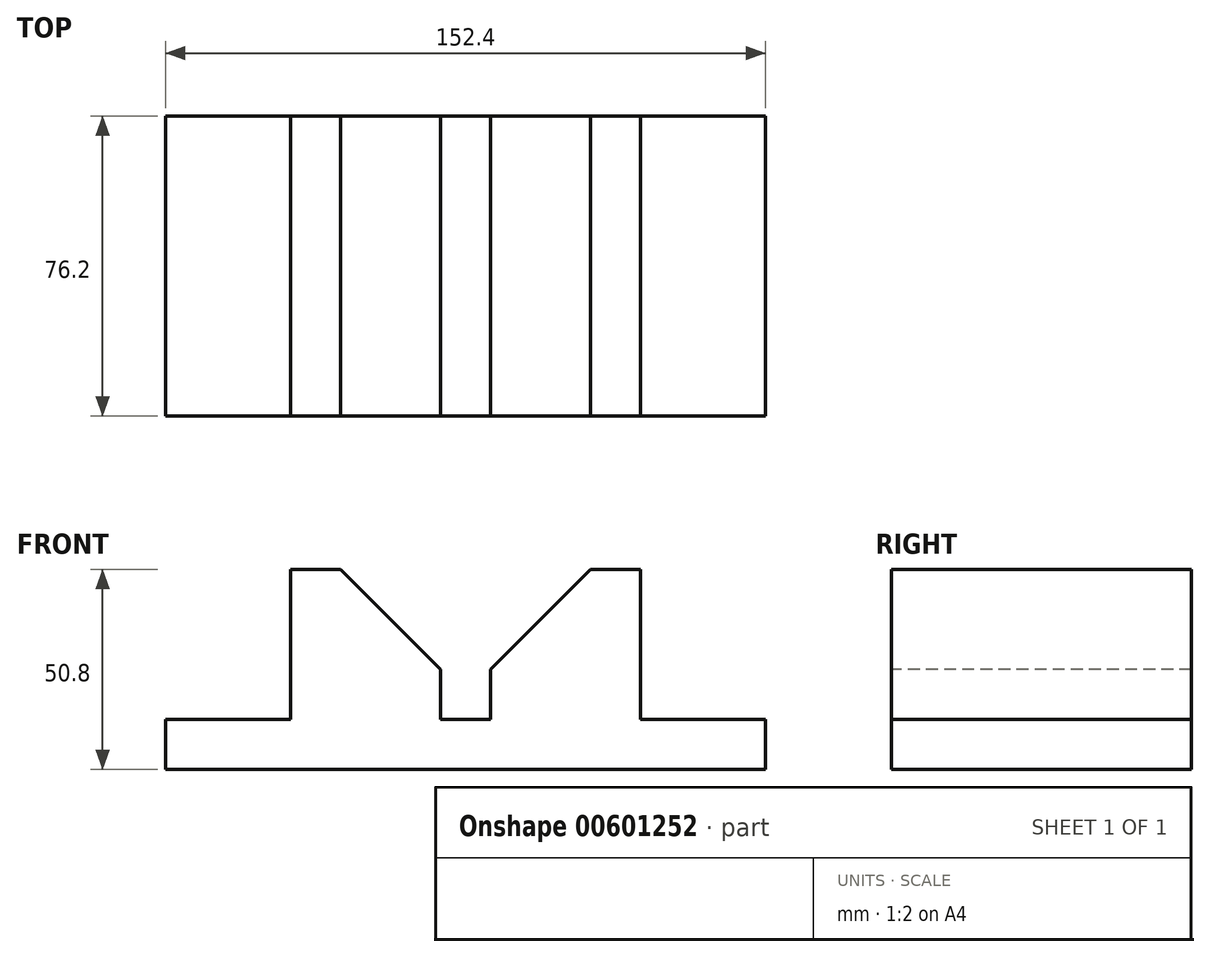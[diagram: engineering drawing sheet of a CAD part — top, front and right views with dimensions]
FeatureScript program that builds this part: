
annotation { "Feature Type Name" : "Feature", "Feature Type Description" : "" }
export const myFeature = defineFeature(function(context is Context, id is Id, definition is map)
    precondition{}
    {
        {
            var Q0;
            Q0=qCreatedBy(makeId("Front.planeOp"),FACE);
            var sketch = newSketch(context, id + "F0", { "sketchPlane" : qUnion([Q0])});
            skLineSegment(sketch, "E0", {"start": v(0, 0) * mm, "end": v(152.4, 0) * mm});
            skLineSegment(sketch, "E1", {"start": v(152.4, 0) * mm, "end": v(152.4, 50.8) * mm});
            skLineSegment(sketch, "E2", {"start": v(152.4, 50.8) * mm, "end": v(0, 50.8) * mm});
            skLineSegment(sketch, "E3", {"start": v(0, 50.8) * mm, "end": v(0, 0) * mm});
            skSolve(sketch);
        }
        {
            var Q0;
            Q0=makeQuery(id+"F0.imprint","IMPRINT",FACE,{"disambiguationData":[TD([[makeQuery(id+"F0.imprint","IMPRINT",EDGE,{"derivedFrom":sQuery(id+"F0.wireOp",EDGE,"E0")}),1.0]])]});
            extrude(context, id + "F1", {"entities" : qUnion([Q0]), "depth" : 76.2 * mm, "offsetDistance" : 25.4 * mm});
        }
        {
            var Q0;
            Q0=makeQuery(id+"F1.opExtrude","SWEPT_FACE",FACE,{"disambiguationData":[OSD([sQuery(id+"F0.wireOp",EDGE,"E2")])]});
            var sketch = newSketch(context, id + "F2", { "sketchPlane" : qUnion([Q0])});
            skLineSegment(sketch, "E4", {"start": v(0, 0) * mm, "end": v(31.75, 0) * mm});
            skLineSegment(sketch, "E5", {"start": v(31.75, 0) * mm, "end": v(31.75, -76.2) * mm});
            skLineSegment(sketch, "E6", {"start": v(152.4, 0) * mm, "end": v(120.65, 0) * mm});
            skLineSegment(sketch, "E7", {"start": v(120.65, 0) * mm, "end": v(120.65, -76.2) * mm});
            skLineSegment(sketch, "E8", {"start": v(31.75, 0) * mm, "end": v(44.45, 0) * mm});
            skLineSegment(sketch, "E9", {"start": v(44.45, 0) * mm, "end": v(44.45, -76.2) * mm});
            skLineSegment(sketch, "E10", {"start": v(120.65, 0) * mm, "end": v(107.95, 0) * mm});
            skLineSegment(sketch, "E11", {"start": v(107.95, 0) * mm, "end": v(107.95, -76.2) * mm});
            skSolve(sketch);
        }
        {
            var Q0;
            Q0 = qSketchRegion(id + "F2", true);
            var Q1;
            Q1=makeQuery(id+"F2.imprint","IMPRINT",FACE,{"disambiguationData":[TD([[makeQuery(id+"F2.imprint","IMPRINT",EDGE,{"derivedFrom":sQuery(id+"F2.wireOp",EDGE,"E4")}),1.0]])]});
            var Q2;
            Q2=makeQuery(id+"F2.imprint","IMPRINT",FACE,{"disambiguationData":[TD([[makeQuery(id+"F2.imprint","IMPRINT",EDGE,{"derivedFrom":sQuery(id+"F2.wireOp",EDGE,"E6")}),1.0]])]});
            extrude(context, id + "F3", {"entities" : qUnion([Q0, Q1, Q2]), "operationType" : NewBodyOperationType.REMOVE, "oppositeDirection" : true, "depth" : 38.1 * mm, "offsetDistance" : 25.4 * mm});
        }
        {
            var Q0;
            Q0=makeQuery(id+"F1.opExtrude","SWEPT_FACE",FACE,{"disambiguationData":[OSD([sQuery(id+"F0.wireOp",EDGE,"E2")])]});
            var sketch = newSketch(context, id + "F4", { "sketchPlane" : qUnion([Q0])});
            skLineSegment(sketch, "E12", {"start": v(76.2, 0) * mm, "end": v(82.55, 0) * mm});
            skLineSegment(sketch, "E13", {"start": v(82.55, 0) * mm, "end": v(82.55, -76.2) * mm});
            skLineSegment(sketch, "E14", {"start": v(76.2, 0) * mm, "end": v(69.85, 0) * mm});
            skLineSegment(sketch, "E15", {"start": v(69.85, 0) * mm, "end": v(69.85, -76.2) * mm});
            skSolve(sketch);
        }
        {
            var Q0;
            Q0 = qSketchRegion(id + "F4", true);
            var Q1;
            Q1=makeQuery(id+"F4.imprint","IMPRINT",FACE,{"disambiguationData":[TD([[makeQuery(id+"F4.imprint","IMPRINT",EDGE,{"derivedFrom":sQuery(id+"F4.wireOp",EDGE,"E12")}),1.0]])]});
            extrude(context, id + "F5", {"entities" : qUnion([Q0, Q1]), "operationType" : NewBodyOperationType.REMOVE, "oppositeDirection" : true, "depth" : 38.1 * mm, "offsetDistance" : 25.4 * mm});
        }
        {
            var Q0;
            Q0=makeQuery(id+"F1.opExtrude","CAP_FACE",FACE,{"disambiguationData":[OSD([sQuery(id+"F0.wireOp",EDGE,"E0"),sQuery(id+"F0.wireOp",EDGE,"E1"),sQuery(id+"F0.wireOp",EDGE,"E2"),sQuery(id+"F0.wireOp",EDGE,"E3")])],"isStart":false});
            var sketch = newSketch(context, id + "F6", { "sketchPlane" : qUnion([Q0])});
            skLineSegment(sketch, "E16", {"start": v(31.75, 50.8) * mm, "end": v(44.45, 50.8) * mm});
            skLineSegment(sketch, "E17", {"start": v(69.85, 12.7) * mm, "end": v(69.85, 25.4) * mm});
            skLineSegment(sketch, "E18", {"start": v(44.45, 50.8) * mm, "end": v(69.85, 25.4) * mm});
            skLineSegment(sketch, "E19", {"start": v(120.65, 50.8) * mm, "end": v(107.95, 50.8) * mm});
            skLineSegment(sketch, "E20", {"start": v(82.55, 12.7) * mm, "end": v(82.55, 25.4) * mm});
            skLineSegment(sketch, "E21", {"start": v(107.95, 50.8) * mm, "end": v(82.55, 25.4) * mm});
            skSolve(sketch);
        }
        {
            var Q0;
            Q0 = qSketchRegion(id + "F6", true);
            var Q1;
            {var subQ0=sQuery(id+"F6.wireOp",EDGE,"E18");Q1=makeQuery(id+"F6.imprint","IMPRINT",FACE,{"disambiguationData":[TD([[makeQuery(id+"F6.imprint","IMPRINT",EDGE,{"derivedFrom":subQ0}),1.0]])]});}
            var Q2;
            {var subQ0=sQuery(id+"F6.wireOp",EDGE,"E21");Q2=makeQuery(id+"F6.imprint","IMPRINT",FACE,{"disambiguationData":[TD([[makeQuery(id+"F6.imprint","IMPRINT",EDGE,{"derivedFrom":subQ0}),-1.0]])]});}
            extrude(context, id + "F7", {"entities" : qUnion([Q0, Q1, Q2]), "operationType" : NewBodyOperationType.REMOVE, "oppositeDirection" : true, "depth" : 87.38 * mm, "offsetDistance" : 25.4 * mm});
        }
    });
